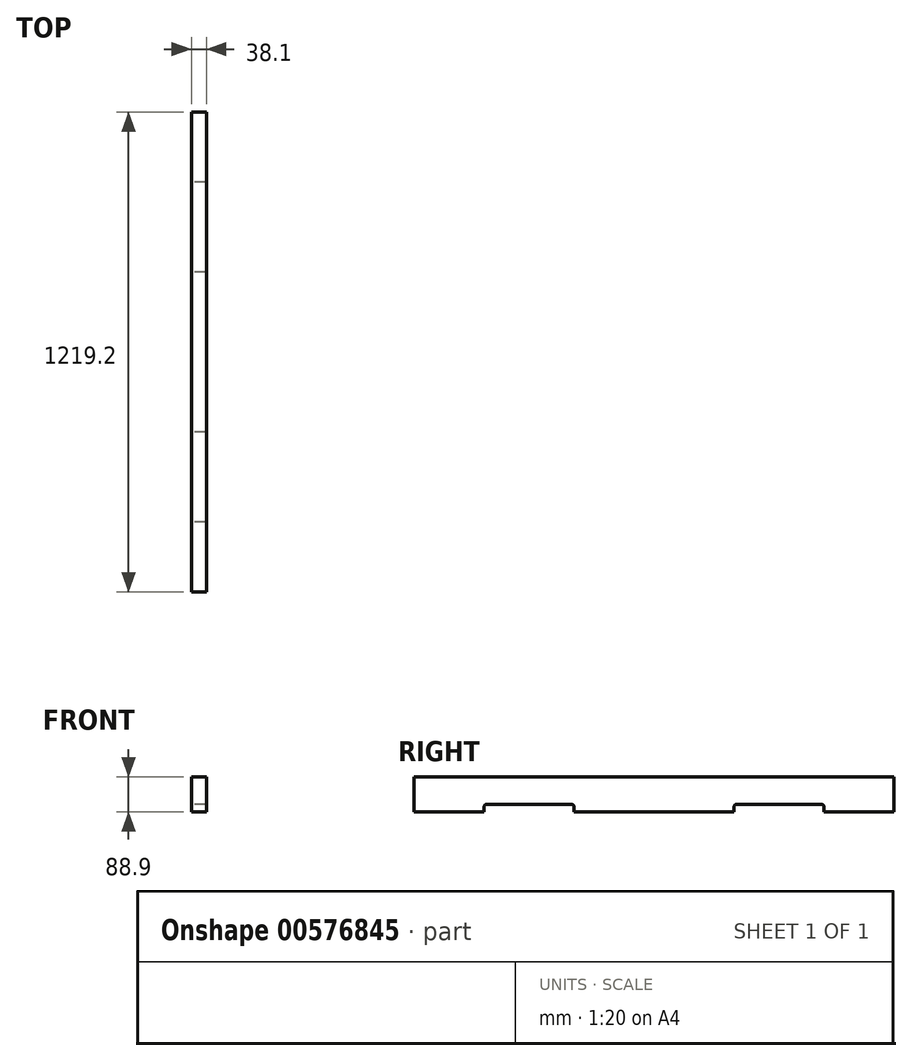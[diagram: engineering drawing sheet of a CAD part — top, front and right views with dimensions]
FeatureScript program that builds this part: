
annotation { "Feature Type Name" : "Feature", "Feature Type Description" : "" }
export const myFeature = defineFeature(function(context is Context, id is Id, definition is map)
    precondition{}
    {
        {
            var Q0;
            Q0=qCreatedBy(makeId("Front.planeOp"),FACE);
            var sketch = newSketch(context, id + "F0", { "sketchPlane" : qUnion([Q0])});
            skLineSegment(sketch, "E0.bottom", {"start": v(0, 0) * mm, "end": v(38.1, 0) * mm});
            skLineSegment(sketch, "E0.top", {"start": v(0, 88.9) * mm, "end": v(38.1, 88.9) * mm});
            skLineSegment(sketch, "E0.left", {"start": v(0, 0) * mm, "end": v(0, 88.9) * mm});
            skLineSegment(sketch, "E0.right", {"start": v(38.1, 0) * mm, "end": v(38.1, 88.9) * mm});
            skSolve(sketch);
        }
        {
            var Q0;
            Q0 = qSketchRegion(id + "F0", true);
            extrude(context, id + "F1", {"entities" : qUnion([Q0]), "oppositeDirection" : true, "depth" : 1219.2 * mm, "offsetDistance" : 25.4 * mm});
        }
        {
            var Q0;
            Q0=makeQuery(id+"F1.opExtrude","SWEPT_FACE",FACE,{"disambiguationData":[OSD([sQuery(id+"F0.wireOp",EDGE,"E0.left")])]});
            var sketch = newSketch(context, id + "F2", { "sketchPlane" : qUnion([Q0])});
            skLineSegment(sketch, "E1", {"start": v(-1219.2, 0) * mm, "end": v(-1219.2, 221.82) * mm, "construction": true});
            skLineSegment(sketch, "E2", {"start": v(0, 0) * mm, "end": v(0, 206.56) * mm, "construction": true});
            skLineSegment(sketch, "E3.bottom", {"start": v(-1041.4, 0) * mm, "end": v(-812.8, 0) * mm});
            skLineSegment(sketch, "E3.top", {"start": v(-1035.05, 19.05) * mm, "end": v(-819.15, 19.05) * mm});
            skLineSegment(sketch, "E3.left", {"start": v(-1041.4, 0) * mm, "end": v(-1041.4, 12.7) * mm});
            skLineSegment(sketch, "E3.right", {"start": v(-812.8, 0) * mm, "end": v(-812.8, 12.7) * mm});
            skLineSegment(sketch, "E4.bottom", {"start": v(-406.4, 0) * mm, "end": v(-177.8, 0) * mm});
            skLineSegment(sketch, "E4.top", {"start": v(-400.05, 19.05) * mm, "end": v(-184.15, 19.05) * mm});
            skLineSegment(sketch, "E4.left", {"start": v(-406.4, 0) * mm, "end": v(-406.4, 12.7) * mm});
            skLineSegment(sketch, "E4.right", {"start": v(-177.8, 0) * mm, "end": v(-177.8, 12.7) * mm});
            skPoint(sketch, "E5.visualSharp", {"position": v(-1041.4, 19.05) * mm});
            skArc(sketch, "E5.filletArc", {"start": v(-1035.05, 19.05) * mm, "mid": v(-1039.54, 17.2) * mm, "end": v(-1041.4, 12.7) * mm});
            skPoint(sketch, "E6.visualSharp", {"position": v(-812.8, 19.05) * mm});
            skArc(sketch, "E6.filletArc", {"start": v(-812.8, 12.7) * mm, "mid": v(-814.66, 17.2) * mm, "end": v(-819.15, 19.05) * mm});
            skPoint(sketch, "E7.visualSharp", {"position": v(-406.4, 19.05) * mm});
            skArc(sketch, "E7.filletArc", {"start": v(-400.05, 19.05) * mm, "mid": v(-404.54, 17.2) * mm, "end": v(-406.4, 12.7) * mm});
            skPoint(sketch, "E8.visualSharp", {"position": v(-177.8, 19.05) * mm});
            skArc(sketch, "E8.filletArc", {"start": v(-177.8, 12.7) * mm, "mid": v(-179.66, 17.2) * mm, "end": v(-184.15, 19.05) * mm});
            skSolve(sketch);
        }
        {
            var Q0;
            Q0 = qSketchRegion(id + "F2", true);
            extrude(context, id + "F3", {"entities" : qUnion([Q0]), "operationType" : NewBodyOperationType.REMOVE, "oppositeDirection" : true, "depth" : 1092.2 * mm, "offsetDistance" : 25.4 * mm});
        }
    });
